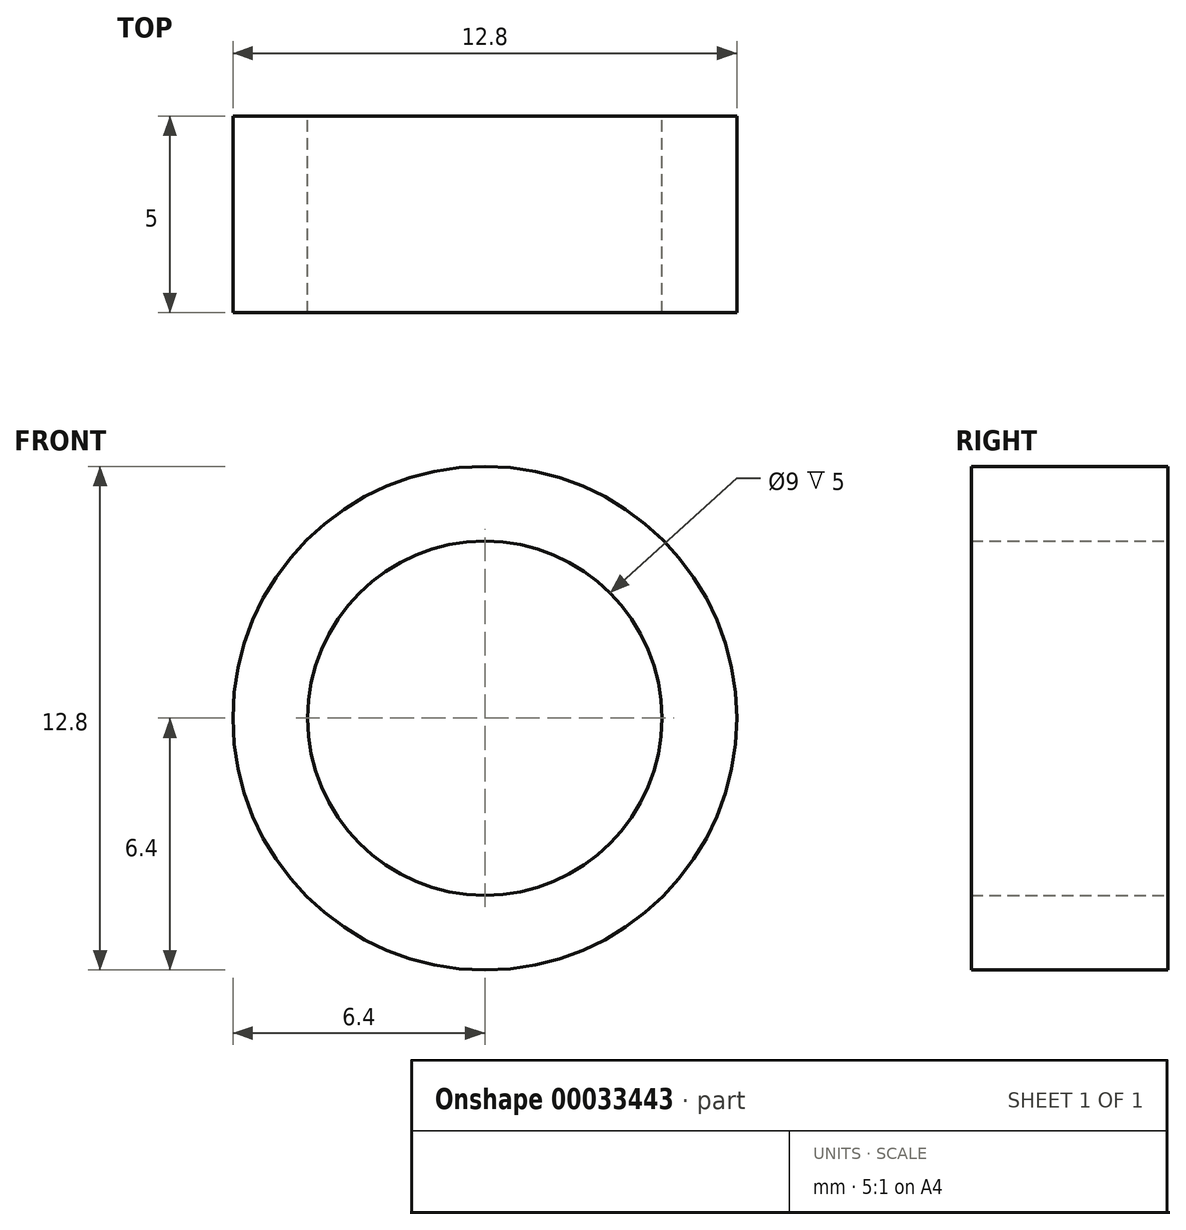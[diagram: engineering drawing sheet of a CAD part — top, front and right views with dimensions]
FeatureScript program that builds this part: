
annotation { "Feature Type Name" : "Feature", "Feature Type Description" : "" }
export const myFeature = defineFeature(function(context is Context, id is Id, definition is map)
    precondition{}
    {
        {
            var Q0;
            Q0=qCreatedBy(makeId("Front.planeOp"),FACE);
            var sketch = newSketch(context, id + "F0", { "sketchPlane" : qUnion([Q0])});
            skCircle(sketch, "E0", {"center": v(0, 0) * mm, "radius": 6.4 * mm});
            skCircle(sketch, "E1", {"center": v(0, 0) * mm, "radius": 4.5 * mm});
            skSolve(sketch);
        }
        {
            var Q0;
            Q0=makeQuery(id+"F0.imprint","IMPRINT",FACE,{"disambiguationData":[TD([[makeQuery(id+"F0.imprint","IMPRINT",EDGE,{"derivedFrom":sQuery(id+"F0.wireOp",EDGE,"E0")}),1.0]])]});
            extrude(context, id + "F1", {"entities" : qUnion([Q0]), "depth" : 5 * mm});
        }
    });
